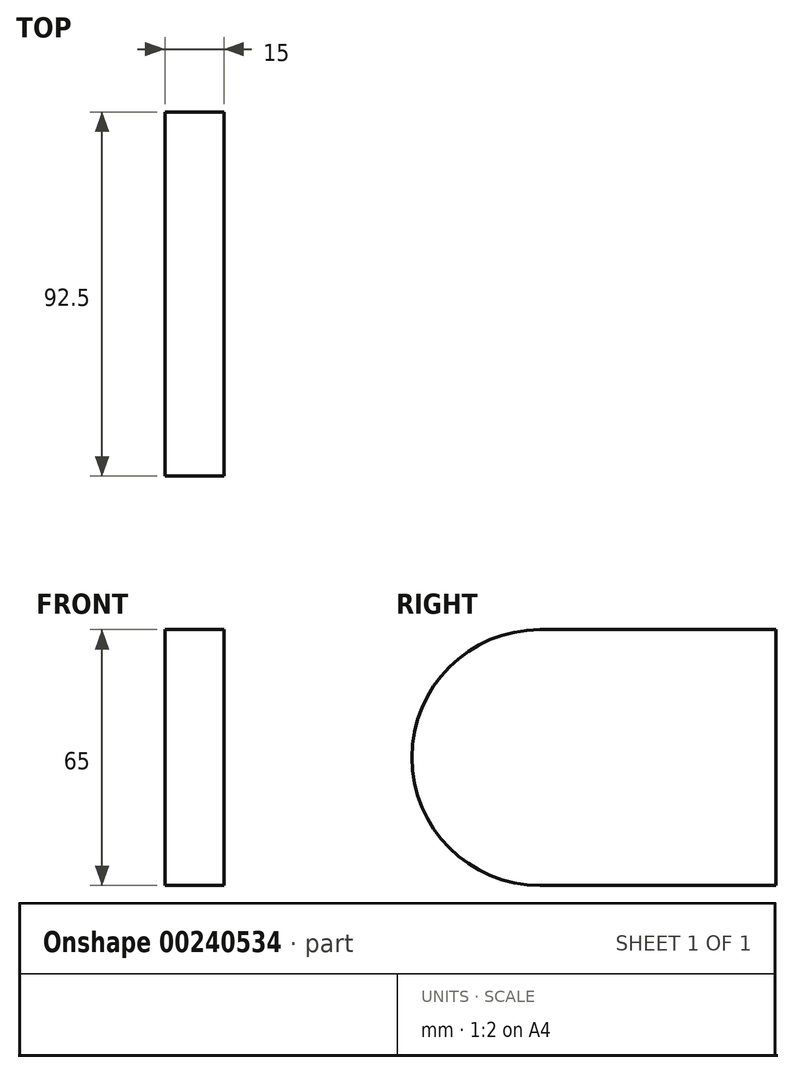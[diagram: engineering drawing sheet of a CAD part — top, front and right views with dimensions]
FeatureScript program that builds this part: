
annotation { "Feature Type Name" : "Feature", "Feature Type Description" : "" }
export const myFeature = defineFeature(function(context is Context, id is Id, definition is map)
    precondition{}
    {
        {
            var Q0;
            Q0=qCreatedBy(makeId("Right.planeOp"),FACE);
            var sketch = newSketch(context, id + "F0", { "sketchPlane" : qUnion([Q0])});
            skLineSegment(sketch, "E0", {"start": v(-0.2, 31.96) * mm, "end": v(59.8, 31.96) * mm});
            skLineSegment(sketch, "E1", {"start": v(59.8, 31.96) * mm, "end": v(59.8, -33.04) * mm});
            skLineSegment(sketch, "E2", {"start": v(59.8, -33.04) * mm, "end": v(-0.2, -33.04) * mm});
            skArc(sketch, "E3", {"start": v(-0.2, 31.96) * mm, "mid": v(-32.7, -0.54) * mm, "end": v(-0.2, -33.04) * mm});
            skSolve(sketch);
        }
        {
            var Q0;
            Q0 = qSketchRegion(id + "F0", true);
            extrude(context, id + "F1", {"entities" : qUnion([Q0]), "depth" : 15 * mm});
        }
    });
